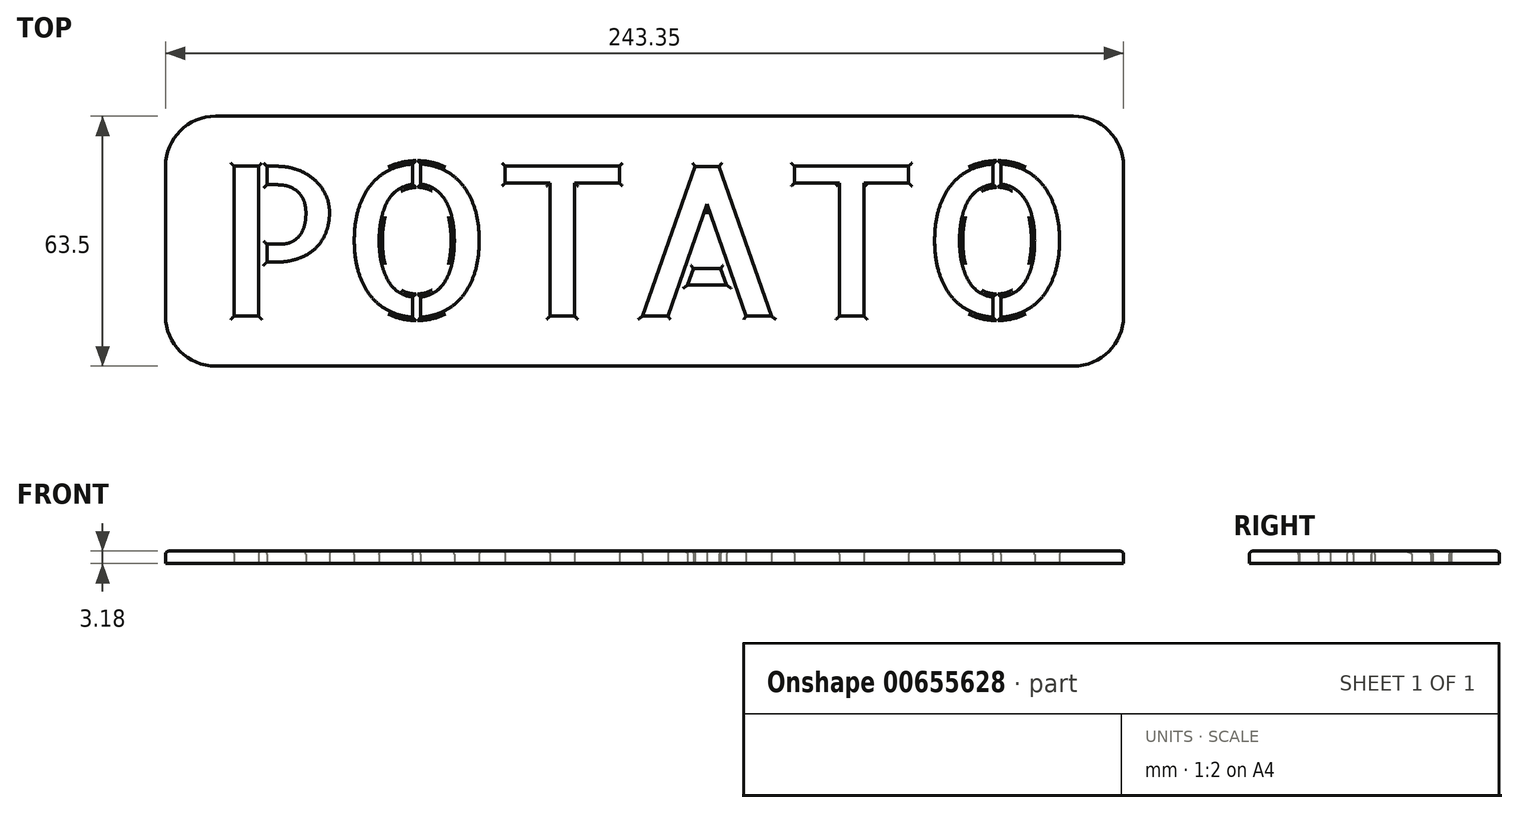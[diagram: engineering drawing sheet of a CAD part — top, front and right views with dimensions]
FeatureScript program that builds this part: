
annotation { "Feature Type Name" : "Feature", "Feature Type Description" : "" }
export const myFeature = defineFeature(function(context is Context, id is Id, definition is map)
    precondition{}
    {
        {
            var Q0;
            Q0=qCreatedBy(makeId("Top.planeOp"),FACE);
            var sketch = newSketch(context, id + "F0", { "sketchPlane" : qUnion([Q0])});
            skLineSegment(sketch, "E0.bottom", {"start": v(12.7, 0) * mm, "end": v(230.65, 0) * mm});
            skLineSegment(sketch, "E0.top", {"start": v(12.7, 63.5) * mm, "end": v(230.65, 63.5) * mm});
            skLineSegment(sketch, "E0.left", {"start": v(0, 12.7) * mm, "end": v(0, 50.8) * mm});
            skLineSegment(sketch, "E0.right", {"start": v(243.35, 12.7) * mm, "end": v(243.35, 50.8) * mm});
            skPoint(sketch, "E1.visualSharp", {"position": v(0, 63.5) * mm});
            skArc(sketch, "E1.filletArc", {"start": v(12.7, 63.5) * mm, "mid": v(3.72, 59.78) * mm, "end": v(0, 50.8) * mm});
            skPoint(sketch, "E2.visualSharp", {"position": v(0, 0) * mm});
            skArc(sketch, "E2.filletArc", {"start": v(0, 12.7) * mm, "mid": v(3.72, 3.72) * mm, "end": v(12.7, 0) * mm});
            skPoint(sketch, "E3.visualSharp", {"position": v(243.35, 0) * mm});
            skArc(sketch, "E3.filletArc", {"start": v(230.65, 0) * mm, "mid": v(239.63, 3.72) * mm, "end": v(243.35, 12.7) * mm});
            skPoint(sketch, "E4.visualSharp", {"position": v(243.35, 63.5) * mm});
            skArc(sketch, "E4.filletArc", {"start": v(243.35, 50.8) * mm, "mid": v(239.63, 59.78) * mm, "end": v(230.65, 63.5) * mm});
            skSolve(sketch);
        }
        {
            var Q0;
            Q0 = qSketchRegion(id + "F0", true);
            extrude(context, id + "F1", {"entities" : qUnion([Q0]), "depth" : 3.17 * mm, "offsetDistance" : 25.4 * mm});
        }
        {
            var Q0;
            Q0=qCreatedBy(makeId("Top.planeOp"),FACE);
            var sketch = newSketch(context, id + "F2", { "sketchPlane" : qUnion([Q0])});
            skText(sketch, "E5", { "text": "POTATO", "fontName": "AllertaStencil-Regular.ttf"});
            const initialGuessF2  = {"E5": [0.0127, 0.0127, 1, 0, 0.0381]};
            skSetInitialGuess(sketch, initialGuessF2);
            skSolve(sketch);
        }
        {
            var Q0;
            Q0 = qSketchRegion(id + "F2", true);
            extrude(context, id + "F3", {"entities" : qUnion([Q0]), "operationType" : NewBodyOperationType.REMOVE, "endBound" : BoundingType.THROUGH_ALL, "depth" : 25.4 * mm, "offsetDistance" : 25.4 * mm});
        }
        {
            var Q0;
            Q0=makeQuery(id+"F1.opExtrude","CAP_FACE",FACE,{"disambiguationData":[OSD([sQuery(id+"F0.wireOp",EDGE,"E0.bottom"),sQuery(id+"F0.wireOp",EDGE,"E0.top"),sQuery(id+"F0.wireOp",EDGE,"E0.left"),sQuery(id+"F0.wireOp",EDGE,"E0.right"),sQuery(id+"F0.wireOp",EDGE,"E1.filletArc"),sQuery(id+"F0.wireOp",EDGE,"E2.filletArc"),sQuery(id+"F0.wireOp",EDGE,"E3.filletArc"),sQuery(id+"F0.wireOp",EDGE,"E4.filletArc")])],"isStart":false});
            fillet(context, id + "F4", {"entities" : qUnion([Q0]), "radius" : 0.83 * mm, "tangentPropagation" : true, "allowEdgeOverflow" : false});
        }
    });
